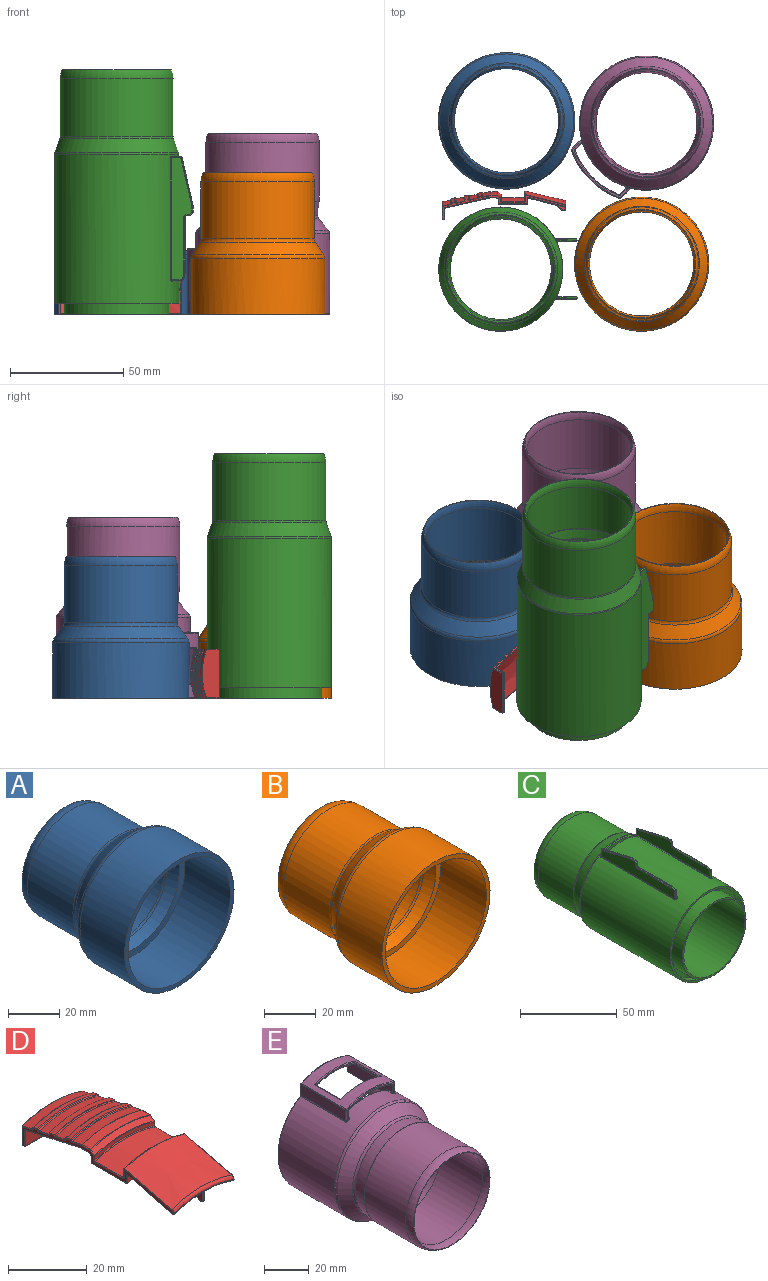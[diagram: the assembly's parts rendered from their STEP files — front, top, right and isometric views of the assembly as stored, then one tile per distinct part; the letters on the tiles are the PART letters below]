
ASSEMBLY  parts=5 mates=4
PART A: 14 faces, bbox 65.2x65.8x65.2 mm
  f0: torus R=23.87mm, axis (0,-1,0), area 51mm2, adj f1,f10
  f1: torus R=16.5mm, axis (0,-1,0), area 645.4mm2, adj f0,f2
  f2: cylinder r=25mm len=50mm, axis (0,-1,0), area 3930.6mm2, adj f1,f11
  f3: cone r=25mm half-angle=36.1deg, axis (0,-1,0), area 1161mm2, adj f11,f12
  f4: cylinder r=30.1mm len=60.2mm, axis (0,-1,0), area 4637.9mm2, adj f5,f12
  f5: plane 60.2x60.2mm, normal (0,-1,0), area 365.7mm2, adj f4,f6
  f6: cylinder r=28.1mm len=56.2mm, axis (0,-1,0), area 4413.9mm2, adj f5,f7
  f7: plane 56.2x56.2mm, normal (0,-1,0), area 517.1mm2, adj f6,f8
  f8: cone r=25mm half-angle=20.8deg, axis (0,-1,0), area 769.2mm2, adj f7,f13
  f9: cylinder r=23mm len=46mm, axis (0,-1,0), area 4035.4mm2, adj f10,f13
  f10: torus R=33mm, axis (0,-1,0), area 560.9mm2, adj f0,f9
  f11: torus R=28mm, axis (0,-1,0), area 299mm2, adj f2,f3
  f12: torus R=27.1mm, axis (0,1,0), area 354.9mm2, adj f3,f4
  f13: torus R=26mm, axis (0,1,0), area 157.9mm2, adj f8,f9
PART B: 14 faces, bbox 64.1x65.8x64.1 mm
  f0: torus R=23.87mm, axis (0,-1,0), area 51mm2, adj f1,f10
  f1: torus R=16.5mm, axis (0,-1,0), area 645.4mm2, adj f0,f2
  f2: cylinder r=25mm len=50mm, axis (0,-1,0), area 3943.1mm2, adj f1,f11
  f3: cone r=25mm half-angle=33.3deg, axis (0,-1,0), area 1128.9mm2, adj f11,f12
  f4: cylinder r=29.6mm len=59.2mm, axis (0,-1,0), area 4575.6mm2, adj f5,f12
  f5: plane 59.2x59.2mm, normal (0,-1,0), area 359.4mm2, adj f4,f6
  f6: cylinder r=27.6mm len=55.2mm, axis (0,-1,0), area 4335.4mm2, adj f5,f7
  f7: plane 55.2x55.2mm, normal (0,-1,0), area 429.6mm2, adj f6,f8
  f8: cone r=25mm half-angle=20.8deg, axis (0,-1,0), area 769.2mm2, adj f7,f13
  f9: cylinder r=23mm len=46mm, axis (0,-1,0), area 4035.4mm2, adj f10,f13
  f10: torus R=33mm, axis (0,-1,0), area 560.9mm2, adj f0,f9
  f11: torus R=28mm, axis (0,-1,0), area 275.8mm2, adj f2,f3
  f12: torus R=26.6mm, axis (0,1,0), area 322.6mm2, adj f3,f4
  f13: torus R=26mm, axis (0,1,0), area 157.9mm2, adj f8,f9
PART C: 133 faces, bbox 59.3x111.3x68.5 mm
  f0: cylinder r=27.4mm len=65.67mm, axis (0,-1,0), area 11028.7mm2, adj f19,f36,f37,f38,f39,f70,f75,f76
  f1: cylinder r=32.78mm len=24.83mm, axis (0,-1,0), area 11mm2, adj f86,f94,f95,f96
  f2: cylinder r=32.78mm len=24.83mm, axis (0,-1,0), area 11mm2, adj f42,f50,f51,f52
  f3: plane 53.7x8.13mm, normal (1,0,0), area 284.6mm2, adj f43,f47,f52,f53,f61,f62,f66,f71
  f4: plane 53.7x9.02mm, normal (-1,0,0), area 331.5mm2, adj f41,f46,f49,f50,f59,f60,f65,f68
  f5: plane 4x0.4mm, normal (0,-1,0), area 1.5mm2, adj f34,f69,f70,f71
  f6: plane 53.7x8.13mm, normal (-1,0,0), area 284.6mm2, adj f85,f90,f93,f94,f103,f104,f109,f112
  f7: plane 53.7x9.02mm, normal (1,0,0), area 331.5mm2, adj f87,f91,f96,f97,f105,f106,f110,f115
  f8: plane 4x0.4mm, normal (0,-1,0), area 1.5mm2, adj f29,f113,f114,f115
  f9: plane 1.7x0.4mm, normal (0,-1,0), area 0.6mm2, adj f41,f42,f43,f44
  f10: plane 1.7x0.4mm, normal (0,-1,0), area 0.6mm2, adj f85,f86,f87,f88
  f11: cylinder r=22.25mm len=76.62mm, axis (0,-1,0), area 10711.8mm2, adj f23,f129
  f12: cone r=22.25mm half-angle=8.5deg, axis (0,1,0), area 676.3mm2, adj f129,f130
  f13: cylinder r=23mm len=46mm, axis (0,-1,0), area 3225.3mm2, adj f14,f130
  f14: torus R=33mm, axis (0,-1,0), area 560.9mm2, adj f13,f15
  f15: torus R=23.87mm, axis (0,-1,0), area 51mm2, adj f14,f16
  f16: torus R=16.5mm, axis (0,-1,0), area 645.4mm2, adj f15,f17
  f17: cylinder r=25mm len=50mm, axis (0,-1,0), area 4031.7mm2, adj f16,f131
  f18: cone r=25mm half-angle=18.9deg, axis (0,-1,0), area 1108.4mm2, adj f131,f132
  f19: plane 54.8x54.8mm, normal (0,-1,0), area 202.1mm2, adj f0,f20
  f20: cylinder r=26.2mm len=52.4mm, axis (0,-1,0), area 658.5mm2, adj f19,f21
  f21: plane 52.4x52.4mm, normal (0,-1,0), area 458.3mm2, adj f20,f22
  f22: cylinder r=23.25mm len=46.5mm, axis (0,-1,0), area 1314.8mm2, adj f21,f23
  f23: plane 46.5x46.5mm, normal (0,-1,0), area 142.9mm2, adj f11,f22
  f24: plane 3.84x0.4mm, normal (0,1,0), area 1.5mm2, adj f117,f122,f125,f128
  f25: cone r=36mm half-angle=12.1deg, axis (0,-1,0), area 9.5mm2, adj f107,f112,f116,f117
  f26: cylinder r=36mm len=2.82mm, axis (0,1,0), area 1.2mm2, adj f98,f103,f106,f107
  f27: cone r=36mm half-angle=38.7deg, axis (0,1,0), area 0.7mm2, adj f88,f93,f97,f98
  f28: cone r=36.3mm half-angle=13.4deg, axis (0,1,0), area 1.1mm2, adj f29,f95,f104,f105
  f29: torus R=31.23mm, axis (0,1,0), area 0.6mm2, adj f8,f28,f109,f110
  f30: plane 3.84x0.4mm, normal (0,1,0), area 1.5mm2, adj f73,f78,f81,f84
  f31: cone r=36mm half-angle=12.1deg, axis (0,-1,0), area 9.5mm2, adj f63,f68,f72,f73
  f32: cylinder r=36mm len=2.82mm, axis (0,1,0), area 1.2mm2, adj f54,f59,f62,f63
  f33: cone r=36mm half-angle=38.7deg, axis (0,1,0), area 0.7mm2, adj f44,f49,f53,f54
  f34: torus R=31.23mm, axis (0,1,0), area 0.6mm2, adj f5,f35,f65,f66
  f35: cone r=36.3mm half-angle=13.4deg, axis (0,1,0), area 1.1mm2, adj f34,f51,f60,f61
  f36: plane 1.7x1.4mm, normal (1,0,0), area 2.4mm2, adj f0,f37,f39,f40
  f37: plane 22x4mm, normal (0,-1,0), area 71.4mm2, adj f0,f36,f38,f40
  f38: plane 1.7x1.4mm, normal (-1,0,0), area 2.4mm2, adj f0,f37,f39,f40
  f39: plane 22x4mm, normal (0,1,0), area 71.4mm2, adj f0,f36,f38,f40
  f40: plane 22x1.4mm, normal (0,0,1), area 30.8mm2, adj f36,f37,f38,f39
  f41: cylinder r=0.4mm len=1.54mm, axis (0,0,1), area 1mm2, adj f4,f9,f45,f46
  f42: torus R=33.18mm, axis (0,1,0), area 0.3mm2, adj f2,f9,f46,f47
  f43: cylinder r=0.4mm len=1.54mm, axis (0,0,1), area 1mm2, adj f3,f9,f47,f48
  f44: torus R=34.61mm, axis (0,1,0), area 0.2mm2, adj f9,f33,f45,f48
  f45: sphere r=0.4mm, area 0.1mm2, adj f41,f44,f49
  f46: bspline ~0.97x0.97mm, area 0.5mm2, adj f4,f41,f42,f50
  f47: bspline ~1.08x0.86mm, area 0.6mm2, adj f3,f42,f43,f52
  f48: sphere r=0.4mm, area 0.2mm2, adj f43,f44,f53
  f49: bspline ~11.03x9.56mm, area 0.8mm2, adj f4,f33,f45,f55
  f50: cylinder r=0.4mm len=24.83mm, axis (0,-1,0), area 11.5mm2, adj f2,f4,f46,f56
  f51: torus R=32.38mm, axis (0,-1,0), area 0mm2, adj f2,f35,f56,f57
  f52: cylinder r=0.4mm len=24.83mm, axis (0,-1,0), area 19.6mm2, adj f2,f3,f47,f57
  f53: bspline ~11.39x9.83mm, area 1.2mm2, adj f3,f33,f48,f58
  f54: torus R=35.6mm, axis (0,-1,0), area 0.1mm2, adj f32,f33,f55,f58
  f55: sphere r=0.4mm, area 0.1mm2, adj f49,f54,f59
  f56: sphere r=0.4mm, area 0mm2, adj f50,f51,f60
  f57: sphere r=0.4mm, area 0.1mm2, adj f51,f52,f61
  f58: sphere r=0.4mm, area 0.2mm2, adj f53,f54,f62
  f59: cylinder r=0.4mm len=2.82mm, axis (0,1,0), area 1.3mm2, adj f4,f32,f55,f64
  f60: bspline ~30.97x8.4mm, area 1.2mm2, adj f4,f35,f56,f65
  f61: bspline ~31.05x8.54mm, area 2mm2, adj f3,f35,f57,f66
  f62: cylinder r=0.4mm len=2.82mm, axis (0,1,0), area 2.2mm2, adj f3,f32,f58,f67
  f63: torus R=35.6mm, axis (0,-1,0), area 0mm2, adj f31,f32,f64,f67
  f64: sphere r=0.4mm, area 0mm2, adj f59,f63,f68
  f65: bspline ~1.26x0.91mm, area 0.6mm2, adj f4,f34,f60,f69
  f66: bspline ~1.51x1mm, area 0.9mm2, adj f3,f34,f61,f71
  f67: sphere r=0.4mm, area 0mm2, adj f62,f63,f72
  f68: bspline ~37.32x9.04mm, area 10.2mm2, adj f4,f31,f64,f74
  f69: cylinder r=0.4mm len=4.27mm, axis (0,0,-1), area 2.5mm2, adj f4,f5,f65,f75
  f70: torus R=27.8mm, axis (0,-1,0), area 0.3mm2, adj f0,f5,f75,f76
  f71: cylinder r=0.4mm len=3.8mm, axis (0,0,1), area 2.3mm2, adj f3,f5,f66,f76
  f72: bspline ~32.89x8.12mm, area 16.9mm2, adj f3,f31,f67,f77
  f73: torus R=31.08mm, axis (0,-1,0), area 0.2mm2, adj f30,f31,f74,f77
  f74: sphere r=0.4mm, area 0.1mm2, adj f68,f73,f78
  f75: bspline ~0.98x0.9mm, area 0.5mm2, adj f0,f69,f70,f79
  f76: bspline ~1.01x0.96mm, area 0.7mm2, adj f0,f70,f71,f80
  f77: sphere r=0.4mm, area 0.3mm2, adj f72,f73,f81
  f78: cylinder r=0.4mm len=4.1mm, axis (0,0,-1), area 2.4mm2, adj f4,f30,f74,f82
  f79: cylinder r=0.4mm len=53.7mm, axis (0,-1,0), area 22.5mm2, adj f0,f4,f75,f82
  f80: cylinder r=0.4mm len=53.7mm, axis (0,-1,0), area 43.2mm2, adj f0,f3,f76,f83
  f81: cylinder r=0.4mm len=3.63mm, axis (0,0,1), area 2.2mm2, adj f3,f30,f77,f83
  f82: bspline ~0.96x0.85mm, area 0.5mm2, adj f0,f78,f79,f84
  f83: bspline ~0.98x0.88mm, area 0.7mm2, adj f0,f80,f81,f84
  f84: torus R=27.8mm, axis (0,-1,0), area 0.3mm2, adj f0,f30,f82,f83
  f85: cylinder r=0.4mm len=1.54mm, axis (0,0,-1), area 1mm2, adj f6,f10,f89,f90
  f86: torus R=33.18mm, axis (0,1,0), area 0.3mm2, adj f1,f10,f90,f91
  f87: cylinder r=0.4mm len=1.54mm, axis (0,0,-1), area 1mm2, adj f7,f10,f91,f92
  f88: torus R=34.61mm, axis (0,1,0), area 0.2mm2, adj f10,f27,f89,f92
  f89: sphere r=0.4mm, area 0.2mm2, adj f85,f88,f93
  f90: bspline ~0.97x0.97mm, area 0.6mm2, adj f6,f85,f86,f94
  f91: bspline ~1.08x0.86mm, area 0.5mm2, adj f7,f86,f87,f96
  f92: sphere r=0.4mm, area 0.1mm2, adj f87,f88,f97
  f93: bspline ~11.39x9.83mm, area 1.2mm2, adj f6,f27,f89,f99
  f94: cylinder r=0.4mm len=24.83mm, axis (0,-1,0), area 19.6mm2, adj f1,f6,f90,f100
  f95: torus R=32.38mm, axis (0,1,0), area 0mm2, adj f1,f28,f100,f101
  f96: cylinder r=0.4mm len=24.83mm, axis (0,-1,0), area 11.5mm2, adj f1,f7,f91,f101
  f97: bspline ~11.03x9.56mm, area 0.8mm2, adj f7,f27,f92,f102
  f98: torus R=35.6mm, axis (0,-1,0), area 0.1mm2, adj f26,f27,f99,f102
  f99: sphere r=0.4mm, area 0.2mm2, adj f93,f98,f103
  f100: sphere r=0.4mm, area 0.1mm2, adj f94,f95,f104
  f101: sphere r=0.4mm, area 0mm2, adj f95,f96,f105
  f102: sphere r=0.4mm, area 0.1mm2, adj f97,f98,f106
  f103: cylinder r=0.4mm len=2.82mm, axis (0,1,0), area 2.2mm2, adj f6,f26,f99,f108
  f104: bspline ~31.05x8.54mm, area 2mm2, adj f6,f28,f100,f109
  f105: bspline ~30.97x8.4mm, area 1.2mm2, adj f7,f28,f101,f110
  f106: cylinder r=0.4mm len=2.82mm, axis (0,1,0), area 1.3mm2, adj f7,f26,f102,f111
  f107: torus R=35.6mm, axis (0,-1,0), area 0mm2, adj f25,f26,f108,f111
  f108: sphere r=0.4mm, area 0mm2, adj f103,f107,f112
  f109: bspline ~1.51x1mm, area 0.9mm2, adj f6,f29,f104,f113
  f110: bspline ~1.28x1mm, area 0.6mm2, adj f7,f29,f105,f115
  f111: sphere r=0.4mm, area 0mm2, adj f106,f107,f116
  f112: bspline ~37.31x9.16mm, area 16.9mm2, adj f6,f25,f108,f118
  f113: cylinder r=0.4mm len=3.8mm, axis (0,0,-1), area 2.3mm2, adj f6,f8,f109,f119
  f114: torus R=27.8mm, axis (0,-1,0), area 0.3mm2, adj f0,f8,f119,f120
  f115: cylinder r=0.4mm len=4.27mm, axis (0,0,1), area 2.5mm2, adj f7,f8,f110,f120
  f116: bspline ~32.98x8.01mm, area 10.2mm2, adj f7,f25,f111,f121
  f117: torus R=31.08mm, axis (0,-1,0), area 0.2mm2, adj f24,f25,f118,f121
  f118: sphere r=0.4mm, area 0.3mm2, adj f112,f117,f122
  f119: bspline ~0.98x0.88mm, area 0.7mm2, adj f0,f113,f114,f123
  f120: bspline ~0.96x0.85mm, area 0.5mm2, adj f0,f114,f115,f124
  f121: sphere r=0.4mm, area 0.1mm2, adj f116,f117,f125
  f122: cylinder r=0.4mm len=3.63mm, axis (0,0,-1), area 2.2mm2, adj f6,f24,f118,f126
  f123: cylinder r=0.4mm len=53.7mm, axis (0,-1,0), area 43.2mm2, adj f0,f6,f119,f126
  f124: cylinder r=0.4mm len=53.7mm, axis (0,-1,0), area 22.5mm2, adj f0,f7,f120,f127
  f125: cylinder r=0.4mm len=4.1mm, axis (0,0,1), area 2.4mm2, adj f7,f24,f121,f127
  f126: bspline ~1.01x0.96mm, area 0.7mm2, adj f0,f122,f123,f128
  f127: bspline ~0.98x0.9mm, area 0.5mm2, adj f0,f124,f125,f128
  f128: torus R=27.8mm, axis (0,-1,0), area 0.3mm2, adj f0,f24,f126,f127
  f129: torus R=24.25mm, axis (0,1,0), area 41.6mm2, adj f11,f12
  f130: torus R=21mm, axis (0,-1,0), area 43mm2, adj f12,f13
  f131: torus R=27mm, axis (0,-1,0), area 103.9mm2, adj f17,f18
  f132: torus R=25.4mm, axis (0,1,0), area 113.6mm2, adj f0,f18
PART D: 158 faces, bbox 24.1x85.1x16.3 mm
  f0: plane 5.85x4.32mm, normal (1,0,0), area 10.7mm2, adj f135,f137,f139,f140
  f1: plane 5.85x4.32mm, normal (-1,0,0), area 10.7mm2, adj f135,f136,f137,f139
  f2: plane 21.3x2.01mm, normal (0,-1,0), area 2.9mm2, adj f5,f74,f84,f108,f111,f138,f141
  f3: cone r=30.78mm half-angle=13.4deg, axis (0,1,0), area 359.4mm2, adj f6,f74,f75,f107,f108,f134,f136,f140
  f4: cone r=36.3mm half-angle=13.4deg, axis (0,1,0), area 380.6mm2, adj f5,f93,f101,f106
  f5: torus R=31.23mm, axis (0,-1,0), area 29.2mm2, adj f2,f4,f89,f109
  f6: plane 21.3x4.49mm, normal (0,-1,0), area 58.1mm2, adj f3,f7,f63,f69,f75,f103,f105,f107
  f7: cylinder r=32.1mm len=21.14mm, axis (0,-1,0), area 277.8mm2, adj f6,f8,f63,f103
  f8: plane 21.3x3.93mm, normal (0,1,0), area 46mm2, adj f7,f9,f49,f56,f63,f97,f100,f103
  f9: cone r=34.8mm half-angle=38.7deg, axis (0,1,0), area 19.9mm2, adj f8,f10,f48,f49,f92,f97
  f10: cylinder r=34.8mm len=21.15mm, axis (0,-1,0), area 63mm2, adj f9,f11,f48,f92
  f11: cone r=34.8mm half-angle=12.1deg, axis (0,-1,0), area 439.2mm2, adj f10,f12,f48,f55,f88,f92
  f12: plane 21.3x6.79mm, normal (0,-1,0), area 131mm2, adj f11,f55,f62,f73,f83,f88
  f13: plane 21.3x7.45mm, normal (0,1,0), area 145.5mm2, adj f46,f47,f59,f60
  f14: cone r=32.23mm half-angle=12.1deg, axis (0,-1,0), area 77.9mm2, adj f37,f38,f45,f46
  f15: plane 21.3x1.89mm, normal (0,1,0), area 2.1mm2, adj f33,f36,f37,f156
  f16: cone r=32.73mm half-angle=12.1deg, axis (0,-1,0), area 33.8mm2, adj f151,f152,f155,f156
  f17: cone r=33.49mm half-angle=12.1deg, axis (0,-1,0), area 75.4mm2, adj f114,f115,f118,f119
  f18: plane 21.3x2.03mm, normal (0,1,0), area 6.5mm2, adj f19,f113,f118,f121
  f19: cone r=33.99mm half-angle=12.1deg, axis (0,-1,0), area 45.3mm2, adj f18,f20,f30,f31,f113,f121,f122,f127
  f20: plane 21.3x1.89mm, normal (0,-1,0), area 4.1mm2, adj f19,f122,f126,f127
  f21: cone r=34.74mm half-angle=12.1deg, axis (0,-1,0), area 75.3mm2, adj f125,f126,f130,f131
  f22: plane 21.3x1.76mm, normal (0,1,0), area 2.1mm2, adj f124,f130,f133,f148
  f23: cone r=35.24mm half-angle=12.1deg, axis (0,-1,0), area 33.7mm2, adj f143,f144,f147,f148
  f24: cone r=36mm half-angle=12.1deg, axis (0,-1,0), area 79mm2, adj f39,f40,f51,f52
  f25: cylinder r=36mm len=21.45mm, axis (0,-1,0), area 62.9mm2, adj f50,f51,f65,f66
  f26: cone r=36mm half-angle=38.7deg, axis (0,1,0), area 37.3mm2, adj f64,f65,f77,f78
  f27: plane 21.3x2.87mm, normal (0,-1,0), area 24.5mm2, adj f76,f77,f86,f87
  f28: cylinder r=33.3mm len=21.46mm, axis (0,-1,0), area 218.5mm2, adj f85,f86,f95,f96
  f29: plane 21.3x4.17mm, normal (0,1,0), area 52.7mm2, adj f94,f95,f101,f102
  f30: plane 54x10.62mm, normal (-1,0,0), area 48.6mm2, adj f19,f33,f34,f35,f38,f39,f47,f48
  f31: plane 54x10.62mm, normal (1,0,0), area 48.6mm2, adj f19,f36,f41,f44,f45,f52,f59,f66
  f32: plane 21.3x0.7mm, normal (0,0,-1), area 14.9mm2, adj f60,f61,f72,f73
  f33: cylinder r=0.25mm len=0.25mm, axis (0,0,1), area 0mm2, adj f15,f30,f34,f154
  f34: bspline ~0.65x0.47mm, area 0.2mm2, adj f30,f33,f37,f38
  f35: bspline ~0.71x0.5mm, area 0.2mm2, adj f30,f39,f40,f142
  f36: cylinder r=0.25mm len=0.25mm, axis (0,0,-1), area 0mm2, adj f15,f31,f41,f157
  f37: torus R=32.43mm, axis (0,-1,0), area 7.4mm2, adj f14,f15,f34,f41
  f38: bspline ~28.72x6.74mm, area 1.1mm2, adj f14,f30,f34,f42
  f39: bspline ~35.9x8.27mm, area 1.2mm2, adj f24,f30,f35,f43
  f40: torus R=35.48mm, axis (0,1,0), area 8.4mm2, adj f24,f35,f44,f143
  f41: bspline ~0.63x0.5mm, area 0.2mm2, adj f31,f36,f37,f45
  f42: sphere r=0.25mm, area 0.1mm2, adj f38,f46,f47
  f43: sphere r=0.25mm, area 0mm2, adj f39,f50,f51
  f44: bspline ~0.68x0.49mm, area 0.2mm2, adj f31,f40,f52,f145
  f45: bspline ~33.99x7.95mm, area 1.1mm2, adj f14,f31,f41,f53
  f46: torus R=31.2mm, axis (0,1,0), area 7.4mm2, adj f13,f14,f42,f53
  f47: cylinder r=0.25mm len=5.57mm, axis (0,0,1), area 2.2mm2, adj f13,f30,f42,f54
  f48: cylinder r=0.25mm len=3.04mm, axis (0,-1,0), area 1.4mm2, adj f9,f10,f11,f30,f49,f55
  f49: bspline ~13.45x11.39mm, area 0.5mm2, adj f8,f9,f30,f48,f56
  f50: cylinder r=0.25mm len=2.89mm, axis (0,-1,0), area 0.9mm2, adj f25,f30,f43,f57
  f51: torus R=35.75mm, axis (0,1,0), area 1.1mm2, adj f24,f25,f43,f58
  f52: bspline ~40.09x9.23mm, area 1.2mm2, adj f24,f31,f44,f58
  f53: sphere r=0.25mm, area 0.1mm2, adj f45,f46,f59
  f54: sphere r=0.25mm, area 0.1mm2, adj f47,f60,f61
  f55: bspline ~53.17x12.31mm, area 9.7mm2, adj f11,f12,f30,f48,f62
  f56: cylinder r=0.25mm len=2.35mm, axis (0,0,1), area 0.9mm2, adj f8,f30,f49,f63
  f57: sphere r=0.25mm, area 0mm2, adj f50,f64,f65
  f58: sphere r=0.25mm, area 0mm2, adj f51,f52,f66
  f59: cylinder r=0.25mm len=5.57mm, axis (0,0,-1), area 2.2mm2, adj f13,f31,f53,f67
  f60: cylinder r=0.25mm len=21.3mm, axis (1,0,0), area 8.4mm2, adj f13,f32,f54,f67
  f61: cylinder r=0.25mm len=0.7mm, axis (0,-1,0), area 0.3mm2, adj f30,f32,f54,f68
  f62: cylinder r=0.25mm len=5.08mm, axis (0,0,-1), area 2mm2, adj f12,f30,f55,f68
  f63: cylinder r=0.25mm len=12.9mm, axis (0,-1,0), area 6.1mm2, adj f6,f7,f8,f30,f56,f69
  f64: bspline ~13.77x11.62mm, area 0.6mm2, adj f26,f30,f57,f70
  f65: torus R=35.75mm, axis (0,1,0), area 3.7mm2, adj f25,f26,f57,f71
  f66: cylinder r=0.25mm len=2.89mm, axis (0,-1,0), area 0.9mm2, adj f25,f31,f58,f71
  f67: sphere r=0.25mm, area 0.1mm2, adj f59,f60,f72
  f68: sphere r=0.25mm, area 0.1mm2, adj f61,f62,f73
  f69: cylinder r=0.25mm len=3.15mm, axis (0,0,-1), area 1.1mm2, adj f6,f30,f63,f75
  f70: sphere r=0.25mm, area 0mm2, adj f64,f76,f77
  f71: sphere r=0.25mm, area 0mm2, adj f65,f66,f78
  f72: cylinder r=0.25mm len=0.7mm, axis (0,1,0), area 0.3mm2, adj f31,f32,f67,f79
  f73: cylinder r=0.25mm len=21.3mm, axis (-1,0,0), area 8.4mm2, adj f12,f32,f68,f79
  f74: torus R=31.1mm, axis (0,1,0), area 4.6mm2, adj f2,f3,f80,f138
  f75: bspline ~30.38x7.96mm, area 8.1mm2, adj f3,f6,f30,f69,f80
  f76: cylinder r=0.25mm len=1.19mm, axis (0,0,-1), area 0.5mm2, adj f27,f30,f70,f81
  f77: torus R=34.68mm, axis (0,1,0), area 4.9mm2, adj f26,f27,f70,f82
  f78: bspline ~13.77x11.62mm, area 0.6mm2, adj f26,f31,f71,f82
  f79: sphere r=0.25mm, area 0.1mm2, adj f72,f73,f83
  f80: sphere r=0.25mm, area 0.1mm2, adj f74,f75,f84
  f81: bspline ~0.61x0.6mm, area 0.2mm2, adj f30,f76,f85,f86
  f82: sphere r=0.25mm, area 0mm2, adj f77,f78,f87
  f83: cylinder r=0.25mm len=5.08mm, axis (0,0,1), area 2mm2, adj f12,f31,f79,f88
  f84: cylinder r=0.25mm len=0.25mm, axis (0,0,-1), area 0.1mm2, adj f2,f30,f80,f89
  f85: cylinder r=0.25mm len=10mm, axis (0,-1,0), area 3.1mm2, adj f28,f30,f81,f90
  f86: torus R=33.55mm, axis (0,1,0), area 8.5mm2, adj f27,f28,f81,f91
  f87: cylinder r=0.25mm len=1.19mm, axis (0,0,1), area 0.5mm2, adj f27,f31,f82,f91
  f88: bspline ~53.76x12.45mm, area 9.7mm2, adj f11,f12,f31,f83,f92
  f89: bspline ~1.28x0.99mm, area 0.4mm2, adj f5,f30,f84,f93
  f90: bspline ~0.65x0.61mm, area 0.2mm2, adj f30,f85,f94,f95
  f91: bspline ~0.65x0.61mm, area 0.2mm2, adj f31,f86,f87,f96
  f92: cylinder r=0.25mm len=3.04mm, axis (0,-1,0), area 1.4mm2, adj f9,f10,f11,f31,f88,f97
  f93: bspline ~41.97x10.75mm, area 5.5mm2, adj f4,f30,f89,f98
  f94: cylinder r=0.25mm len=2.56mm, axis (0,0,1), area 1mm2, adj f29,f30,f90,f98
  f95: torus R=33.55mm, axis (0,-1,0), area 8.5mm2, adj f28,f29,f90,f99
  f96: cylinder r=0.25mm len=10mm, axis (0,-1,0), area 3.1mm2, adj f28,f31,f91,f99
  f97: bspline ~13.45x11.39mm, area 0.5mm2, adj f8,f9,f31,f92,f100
  f98: sphere r=0.25mm, area 0.1mm2, adj f93,f94,f101
  f99: bspline ~0.61x0.6mm, area 0.2mm2, adj f31,f95,f96,f102
  f100: cylinder r=0.25mm len=2.35mm, axis (0,0,-1), area 0.9mm2, adj f8,f31,f97,f103
  f101: torus R=35.98mm, axis (0,-1,0), area 9.8mm2, adj f4,f29,f98,f104
  f102: cylinder r=0.25mm len=2.56mm, axis (0,0,-1), area 1mm2, adj f29,f31,f99,f104
  f103: cylinder r=0.25mm len=12.9mm, axis (0,-1,0), area 6.1mm2, adj f6,f7,f8,f31,f100,f105
  f104: sphere r=0.25mm, area 0.1mm2, adj f101,f102,f106
  f105: cylinder r=0.25mm len=3.15mm, axis (0,0,1), area 1.1mm2, adj f6,f31,f103,f107
  f106: bspline ~41.97x10.75mm, area 5.5mm2, adj f4,f31,f104,f109
  f107: bspline ~34.75x9.07mm, area 8.1mm2, adj f3,f6,f31,f105,f110
  f108: torus R=31.1mm, axis (0,1,0), area 4.6mm2, adj f2,f3,f110,f141
  f109: bspline ~1.28x0.99mm, area 0.4mm2, adj f5,f31,f106,f111
  f110: sphere r=0.25mm, area 0.2mm2, adj f107,f108,f111
  f111: cylinder r=0.25mm len=0.25mm, axis (0,0,1), area 0.1mm2, adj f2,f31,f109,f110
  f112: bspline ~0.71x0.5mm, area 0.2mm2, adj f30,f114,f115,f150
  f113: cylinder r=0.25mm len=0.31mm, axis (0,0,1), area 0.1mm2, adj f18,f19,f30,f116
  f114: bspline ~47.53x10.91mm, area 1.1mm2, adj f17,f30,f112,f116
  f115: torus R=32.97mm, axis (0,1,0), area 8.5mm2, adj f17,f112,f117,f151
  f116: bspline ~0.65x0.47mm, area 0.2mm2, adj f30,f113,f114,f118
  f117: bspline ~0.68x0.49mm, area 0.2mm2, adj f31,f115,f119,f153
  f118: torus R=33.69mm, axis (0,-1,0), area 7.4mm2, adj f17,f18,f116,f120
  f119: bspline ~53.02x12.16mm, area 1.1mm2, adj f17,f31,f117,f120
  f120: bspline ~0.63x0.5mm, area 0.2mm2, adj f31,f118,f119,f121
  f121: cylinder r=0.25mm len=0.31mm, axis (0,0,-1), area 0.1mm2, adj f18,f19,f31,f120
  f122: cylinder r=0.25mm len=0.25mm, axis (0,0,-1), area 0.1mm2, adj f19,f20,f30,f123
  f123: bspline ~0.71x0.57mm, area 0.2mm2, adj f30,f122,f125,f126
  f124: cylinder r=0.25mm len=0.25mm, axis (0,0,1), area 0mm2, adj f22,f30,f128,f146
  f125: bspline ~36.92x8.54mm, area 1.1mm2, adj f21,f30,f123,f128
  f126: torus R=34.22mm, axis (0,1,0), area 9.7mm2, adj f20,f21,f123,f129
  f127: cylinder r=0.25mm len=0.25mm, axis (0,0,1), area 0.1mm2, adj f19,f20,f31,f129
  f128: bspline ~0.65x0.47mm, area 0.2mm2, adj f30,f124,f125,f130
  f129: bspline ~0.68x0.65mm, area 0.2mm2, adj f31,f126,f127,f131
  f130: torus R=34.95mm, axis (0,-1,0), area 7.4mm2, adj f21,f22,f128,f132
  f131: bspline ~39.91x9.22mm, area 1.1mm2, adj f21,f31,f129,f132
  f132: bspline ~0.63x0.5mm, area 0.2mm2, adj f31,f130,f131,f133
  f133: cylinder r=0.25mm len=0.25mm, axis (0,0,-1), area 0mm2, adj f22,f31,f132,f149
  f134: bspline ~1.12x1.01mm, area 0.6mm2, adj f3,f135,f136,f140
  f135: cylinder r=0.25mm len=5.45mm, axis (0,-0.74,-0.67), area 5.2mm2, adj f0,f1,f134,f137
  f136: bspline ~38.57x9.41mm, area 2.4mm2, adj f1,f3,f134,f138
  f137: torus R=0.75mm, axis (1,0,0), area 1.6mm2, adj f0,f1,f135,f139
  f138: bspline ~0.62x0.55mm, area 0.2mm2, adj f2,f74,f136,f139
  f139: cylinder r=0.25mm len=2.18mm, axis (0,0,1), area 1.7mm2, adj f0,f1,f137,f138,f141
  f140: bspline ~38.57x9.41mm, area 2.4mm2, adj f0,f3,f134,f141
  f141: bspline ~0.63x0.6mm, area 0.2mm2, adj f2,f108,f139,f140
  f142: sphere r=0.25mm, area 0.1mm2, adj f35,f143,f144
  f143: torus R=35.36mm, axis (0,1,0), area 8.4mm2, adj f23,f40,f142,f145
  f144: bspline ~32.88x7.6mm, area 0.5mm2, adj f23,f30,f142,f146
  f145: sphere r=0.25mm, area 0.1mm2, adj f44,f143,f147
  f146: sphere r=0.25mm, area 0.1mm2, adj f124,f144,f148
  f147: bspline ~32.88x7.6mm, area 0.5mm2, adj f23,f31,f145,f149
  f148: torus R=35.04mm, axis (0,-1,0), area 7.4mm2, adj f22,f23,f146,f149
  f149: sphere r=0.25mm, area 0.1mm2, adj f133,f147,f148
  f150: sphere r=0.25mm, area 0.1mm2, adj f112,f151,f152
  f151: torus R=32.85mm, axis (0,1,0), area 8.4mm2, adj f16,f115,f150,f153
  f152: bspline ~47.1x10.82mm, area 0.5mm2, adj f16,f30,f150,f154
  f153: sphere r=0.25mm, area 0.1mm2, adj f117,f151,f155
  f154: sphere r=0.25mm, area 0.1mm2, adj f33,f152,f156
  f155: bspline ~47.1x10.82mm, area 0.5mm2, adj f16,f31,f153,f157
  f156: torus R=32.53mm, axis (0,-1,0), area 7.4mm2, adj f15,f16,f154,f157
  f157: sphere r=0.25mm, area 0.1mm2, adj f36,f155,f156
PART E: 89 faces, bbox 64.1x83.3x70.2 mm
  f0: plane 64.1x58.4mm, normal (0,1,0), area 209.5mm2, adj f33,f34,f36,f39,f42,f43,f46,f47
  f1: cylinder r=27.6mm len=55.2mm, axis (0,-1,0), area 5254.8mm2, adj f14,f43,f50,f56,f62,f63,f70
  f2: cylinder r=29.6mm len=59.2mm, axis (0,-1,0), area 5734.1mm2, adj f29,f32,f38,f45,f46,f57,f65,f66
  f3: cone r=25mm half-angle=6deg, axis (0,-1,0), area 944mm2, adj f28,f30
  f4: cylinder r=25mm len=50mm, axis (0,-1,0), area 4067.5mm2, adj f5,f28
  f5: torus R=16.5mm, axis (0,-1,0), area 645.4mm2, adj f4,f6
  f6: torus R=23.87mm, axis (0,-1,0), area 51mm2, adj f5,f7
  f7: torus R=33mm, axis (0,-1,0), area 560.9mm2, adj f6,f8
  f8: cylinder r=23mm len=46mm, axis (0,-1,0), area 3776.6mm2, adj f7,f9
  f9: cone r=22.25mm half-angle=6deg, axis (0,-1,0), area 1015.7mm2, adj f8,f10
  f10: cylinder r=22.25mm len=44.5mm, axis (0,-1,0), area 410.6mm2, adj f9,f11
  f11: plane 46.9x46.9mm, normal (0,1,0), area 172.3mm2, adj f10,f12
  f12: cylinder r=23.45mm len=46.9mm, axis (0,-1,0), area 515.7mm2, adj f11,f13
  f13: torus R=24.95mm, axis (0,-1,0), area 355.2mm2, adj f12,f14
  f14: plane 55.2x55.2mm, normal (0,1,0), area 437.5mm2, adj f1,f13
  f15: cone r=24.26mm half-angle=39.7deg, axis (0,1,0), area 1151.3mm2, adj f29,f30
  f16: plane 26.9x4.64mm, normal (0,1,0), area 33.6mm2, adj f63,f64,f74,f75
  f17: plane 28.2x6.47mm, normal (-1,0,0), area 172.6mm2, adj f36,f50,f51,f52,f64,f65,f71
  f18: plane 28.2x6.47mm, normal (1,0,0), area 172.6mm2, adj f54,f62,f69,f74,f77,f78,f80
  f19: plane 28.2x6mm, normal (1,0,0), area 169.3mm2, adj f32,f33,f35,f37
  f20: cylinder r=35.3mm len=30.24mm, axis (0,-1,0), area 448.5mm2, adj f34,f35,f48,f49,f81,f82,f83,f84
  f21: plane 28.2x6mm, normal (-1,0,0), area 169.3mm2, adj f47,f48,f66,f67
  f22: plane 29.9x8.89mm, normal (0,-1,0), area 28.3mm2, adj f37,f45,f49,f51,f60,f67,f68,f73
  f23: cylinder r=33.8mm len=28.2mm, axis (0,-1,0), area 366.7mm2, adj f52,f53,f68,f69,f85,f86,f87,f88
  f24: plane 24.55x2.97mm, normal (0,-1,0), area 17.5mm2, adj f25,f27,f82,f83,f84,f88
  f25: plane 15.79x0.75mm, normal (1,0,0), area 11.8mm2, adj f24,f26,f83,f85,f87,f88
  f26: plane 24.55x2.97mm, normal (0,1,0), area 17.5mm2, adj f25,f27,f81,f82,f83,f85
  f27: plane 15.79x0.75mm, normal (-1,0,0), area 11.8mm2, adj f24,f26,f82,f85,f86,f88
  f28: torus R=23mm, axis (0,1,0), area 33mm2, adj f3,f4
  f29: torus R=27.6mm, axis (0,1,0), area 256.3mm2, adj f2,f15
  f30: torus R=26.34mm, axis (0,-1,0), area 245.4mm2, adj f3,f15
  f31: sphere r=0.4mm, area 0.2mm2, adj f33,f34,f35
  f32: cylinder r=0.4mm len=28.2mm, axis (0,-1,0), area 11.5mm2, adj f2,f19,f38,f39
  f33: cylinder r=0.4mm len=6mm, axis (0,0,1), area 3.8mm2, adj f0,f19,f31,f39
  f34: torus R=34.9mm, axis (0,-1,0), area 19.6mm2, adj f0,f20,f31,f40
  f35: cylinder r=0.4mm len=28.2mm, axis (0,-1,0), area 12.7mm2, adj f19,f20,f31,f44
  f36: cylinder r=0.4mm len=6.47mm, axis (0,0,-1), area 4.1mm2, adj f0,f17,f41,f42
  f37: cylinder r=0.4mm len=6mm, axis (0,0,1), area 3.7mm2, adj f19,f22,f38,f44
  f38: bspline ~0.99x0.96mm, area 0.5mm2, adj f2,f32,f37,f45
  f39: torus R=0.8mm, axis (0,-1,0), area 0.3mm2, adj f0,f32,f33,f46
  f40: sphere r=0.4mm, area 0.2mm2, adj f34,f47,f48
  f41: sphere r=0.4mm, area 0.2mm2, adj f36,f43,f50
  f42: torus R=0.8mm, axis (0,-1,0), area 0.4mm2, adj f0,f36,f52,f53
  f43: torus R=28mm, axis (0,-1,0), area 90.9mm2, adj f0,f1,f41,f55
  f44: sphere r=0.4mm, area 0.2mm2, adj f35,f37,f49
  f45: torus R=30mm, axis (0,-1,0), area 0.5mm2, adj f2,f22,f38,f57
  f46: torus R=29.2mm, axis (0,-1,0), area 95.8mm2, adj f0,f2,f39,f58
  f47: cylinder r=0.4mm len=6mm, axis (0,0,-1), area 3.8mm2, adj f0,f21,f40,f58
  f48: cylinder r=0.4mm len=28.2mm, axis (0,-1,0), area 12.7mm2, adj f20,f21,f40,f59
  f49: torus R=34.9mm, axis (0,-1,0), area 19.6mm2, adj f20,f22,f44,f59
  f50: cylinder r=0.4mm len=24.5mm, axis (0,-1,0), area 10.2mm2, adj f1,f17,f41,f56
  f51: cylinder r=0.4mm len=4.17mm, axis (0,0,-1), area 2.5mm2, adj f17,f22,f57,f60
  f52: cylinder r=0.4mm len=28.2mm, axis (0,-1,0), area 13mm2, adj f17,f23,f42,f60
  f53: torus R=34.2mm, axis (0,-1,0), area 17.7mm2, adj f0,f23,f42,f61
  f54: cylinder r=0.4mm len=6.47mm, axis (0,0,1), area 4.1mm2, adj f0,f18,f55,f61
  f55: sphere r=0.4mm, area 0.2mm2, adj f43,f54,f62
  f56: bspline ~0.98x0.91mm, area 0.5mm2, adj f1,f50,f63,f64
  f57: bspline ~0.99x0.89mm, area 0.7mm2, adj f2,f45,f51,f65
  f58: torus R=0.8mm, axis (0,-1,0), area 0.3mm2, adj f0,f46,f47,f66
  f59: sphere r=0.4mm, area 0.2mm2, adj f48,f49,f67
  f60: torus R=0.8mm, axis (0,-1,0), area 0.4mm2, adj f22,f51,f52,f68
  f61: torus R=0.8mm, axis (0,-1,0), area 0.4mm2, adj f0,f53,f54,f69
  f62: cylinder r=0.4mm len=24.5mm, axis (0,-1,0), area 10.2mm2, adj f1,f18,f55,f70
  f63: torus R=28mm, axis (0,-1,0), area 17.5mm2, adj f1,f16,f56,f70
  f64: cylinder r=0.4mm len=1.82mm, axis (0,0,-1), area 1mm2, adj f16,f17,f56,f71
  f65: cylinder r=0.4mm len=2.9mm, axis (0,-1,0), area 2.4mm2, adj f2,f17,f57,f71
  f66: cylinder r=0.4mm len=28.2mm, axis (0,-1,0), area 11.5mm2, adj f2,f21,f58,f72
  f67: cylinder r=0.4mm len=6mm, axis (0,0,-1), area 3.7mm2, adj f21,f22,f59,f72
  f68: torus R=34.2mm, axis (0,-1,0), area 17.7mm2, adj f22,f23,f60,f73
  f69: cylinder r=0.4mm len=28.2mm, axis (0,-1,0), area 13mm2, adj f18,f23,f61,f73
  f70: bspline ~0.96x0.84mm, area 0.5mm2, adj f1,f62,f63,f74
  f71: bspline ~0.93x0.88mm, area 0.7mm2, adj f17,f64,f65,f75
  f72: bspline ~1.02x0.95mm, area 0.5mm2, adj f2,f66,f67,f76
  f73: torus R=0.8mm, axis (0,-1,0), area 0.4mm2, adj f22,f68,f69,f77
  f74: cylinder r=0.4mm len=1.82mm, axis (0,0,1), area 1mm2, adj f16,f18,f70,f78
  f75: torus R=29.2mm, axis (0,-1,0), area 17.4mm2, adj f2,f16,f71,f78
  f76: torus R=30mm, axis (0,-1,0), area 0.5mm2, adj f2,f22,f72,f79
  f77: cylinder r=0.4mm len=4.17mm, axis (0,0,1), area 2.5mm2, adj f18,f22,f73,f79
  f78: bspline ~0.98x0.96mm, area 0.7mm2, adj f18,f74,f75,f80
  f79: bspline ~1.01x0.96mm, area 0.7mm2, adj f2,f76,f77,f80
  f80: cylinder r=0.4mm len=2.9mm, axis (0,-1,0), area 2.4mm2, adj f2,f18,f78,f79
  f81: torus R=34.9mm, axis (0,1,0), area 16.1mm2, adj f20,f26,f82,f83
  f82: cylinder r=0.4mm len=16.53mm, axis (0,-1,0), area 12.4mm2, adj f20,f24,f26,f27,f81,f84
  f83: cylinder r=0.4mm len=16.53mm, axis (0,-1,0), area 12.4mm2, adj f20,f24,f25,f26,f81,f84
  f84: torus R=34.9mm, axis (0,1,0), area 16.1mm2, adj f20,f24,f82,f83
  f85: torus R=34.2mm, axis (0,1,0), area 15.9mm2, adj f23,f25,f26,f27,f86,f87
  f86: cylinder r=0.4mm len=16.53mm, axis (0,-1,0), area 7.7mm2, adj f23,f27,f85,f88
  f87: cylinder r=0.4mm len=16.53mm, axis (0,-1,0), area 7.7mm2, adj f23,f25,f85,f88
  f88: torus R=34.2mm, axis (0,1,0), area 15.9mm2, adj f23,f24,f25,f27,f86,f87
PLACE A rot(axis=(1,0,0),90deg) t=(-157.67,-21.42,52.28)mm
PLACE B rot(axis=(1,0,0),90deg) t=(-98.09,-84.64,52.28)mm
PLACE C rot(axis=(0.58,0.58,0.58),120deg) t=(-160.23,-86.92,57.28)mm
PLACE D rot(axis=(-0.58,0.58,0.58),120deg) t=(-121.61,-88.54,63.18)mm
PLACE E rot(axis=(-0.28,-0.68,0.68),148.6deg) t=(-95.9,-22.44,87.28)mm
MATE planar D.f31 <-> B.f0  axis (0,0,-1) through (-148.66,-55.1,52.28)mm
MATE planar B.f0 <-> C.f0  axis (0,0,-1) through (-98.09,-84.64,52.28)mm
MATE planar E.f0 <-> A.f0  axis (0,0,-1) through (-95.8,-22.34,52.28)mm
MATE planar A.f0 <-> B.f0  axis (0,0,-1) through (-157.67,-21.42,52.28)mm
